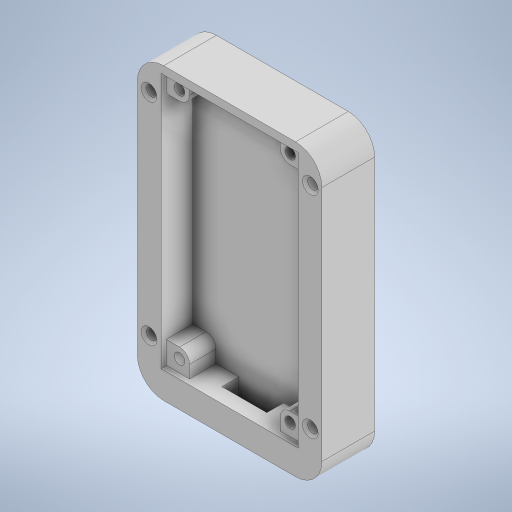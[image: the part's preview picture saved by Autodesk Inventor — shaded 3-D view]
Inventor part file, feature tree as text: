
AUTODESK INVENTOR PART (.ipt)
format: ipt  version: 2023 (Build 270158000, 158)  size: 346,624 bytes
history: native  units: mm
features: extrude x6, sketch x5, other x1, fillet x1, chamfer x1, projected_geometry x1
ambient origin geometry x8: Origin, YZ Plane, XZ Plane, XY Plane, X Axis, Y Axis, Z Axis, Center Point
bodies: Body1 (feature_tree)
feature tree (15):
  other  "솔리드1"
  sketch  "스케치1"
  extrude  "돌출1"  Depth=58.5mm
  extrude  "돌출3"  Depth=35.0mm
  extrude  "돌출4"  Depth=26.0mm
  extrude  "돌출5"  Depth=48.5mm
  extrude  "돌출6"  Depth=3.5mm
  fillet  "모깎기2"  Radius=10.0mm
  extrude  "돌출7"  Depth=1.5mm
  chamfer  "모따기1"  Distance=6.0mm
  sketch  "스케치2"
  sketch  "스케치3"
  projected_geometry  "투영된 루프1"
  sketch  "스케치4"
  sketch  "스케치5"
